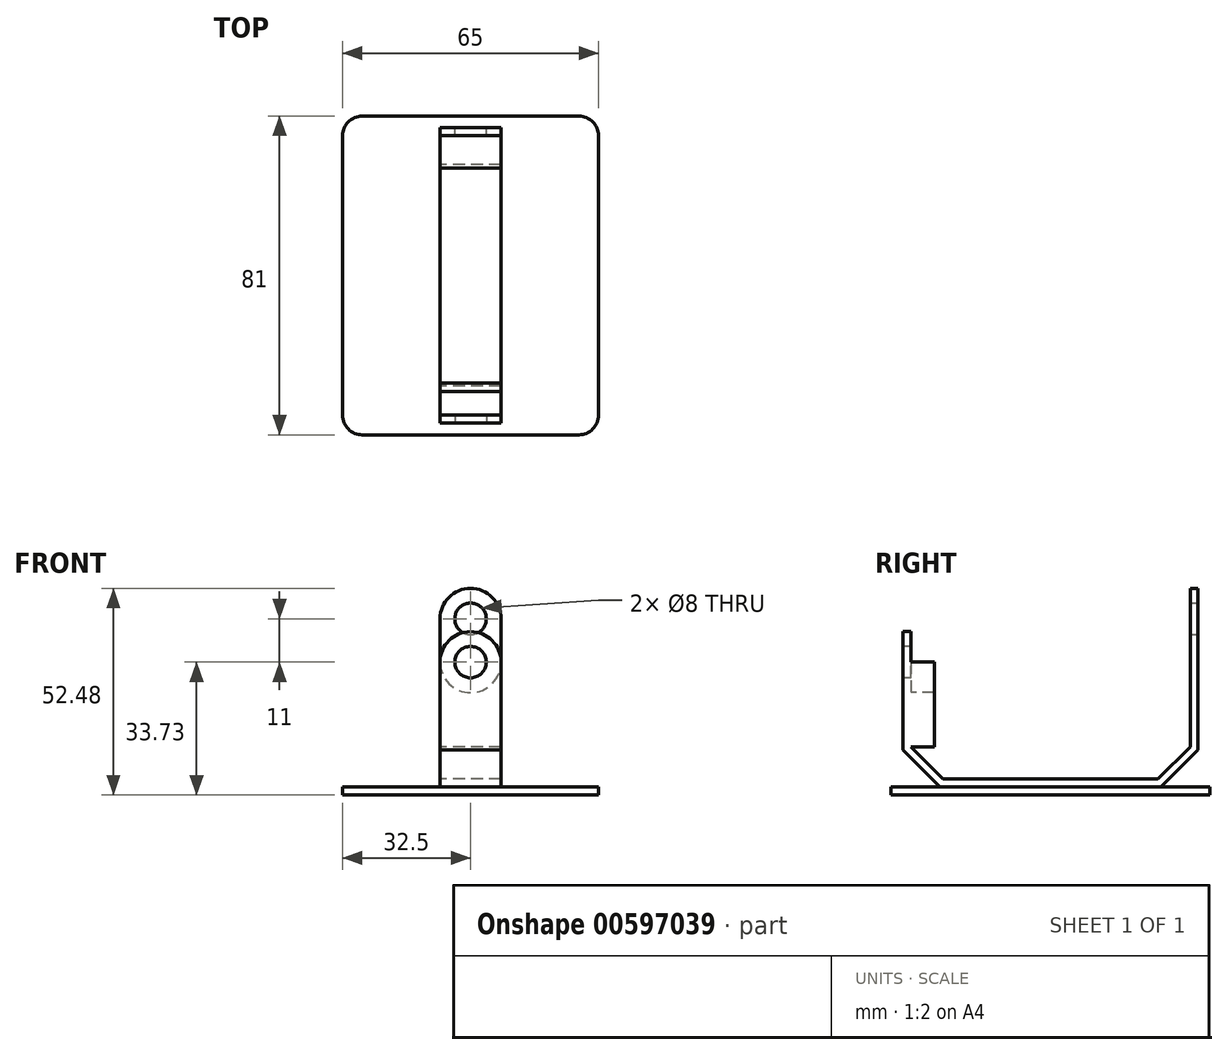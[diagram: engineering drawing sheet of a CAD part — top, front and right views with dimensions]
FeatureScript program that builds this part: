
annotation { "Feature Type Name" : "Feature", "Feature Type Description" : "" }
export const myFeature = defineFeature(function(context is Context, id is Id, definition is map)
    precondition{}
    {
        {
            var Q0;
            Q0=qCreatedBy(makeId("Right.planeOp"),FACE);
            var sketch = newSketch(context, id + "F0", { "sketchPlane" : qUnion([Q0])});
            skLineSegment(sketch, "E0", {"start": v(0, 21.5) * mm, "end": v(0, 0) * mm});
            skLineSegment(sketch, "E1", {"start": v(0, 0) * mm, "end": v(8.23, -8.23) * mm});
            skLineSegment(sketch, "E2", {"start": v(8.23, -8.23) * mm, "end": v(62.77, -8.23) * mm});
            skLineSegment(sketch, "E3", {"start": v(62.77, -8.23) * mm, "end": v(71, 0) * mm});
            skLineSegment(sketch, "E4", {"start": v(71, 0) * mm, "end": v(71, 32.5) * mm});
            skLineSegment(sketch, "E5", {"start": v(0, 21.5) * mm, "end": v(-2, 21.5) * mm});
            skLineSegment(sketch, "E6", {"start": v(73, 32.5) * mm, "end": v(71, 32.5) * mm});
            skLineSegment(sketch, "E7", {"start": v(-2, 21.5) * mm, "end": v(-2, -0.83) * mm});
            skLineSegment(sketch, "E8", {"start": v(-2, -0.83) * mm, "end": v(7.4, -10.23) * mm});
            skLineSegment(sketch, "E9", {"start": v(7.4, -10.23) * mm, "end": v(56.69, -10.23) * mm});
            skLineSegment(sketch, "E10", {"start": v(73, 32.5) * mm, "end": v(73, -0.83) * mm});
            skLineSegment(sketch, "E11", {"start": v(73, -0.83) * mm, "end": v(63.6, -10.23) * mm});
            skLineSegment(sketch, "E12", {"start": v(56.69, -10.23) * mm, "end": v(63.6, -10.23) * mm});
            skSolve(sketch);
        }
        {
            var Q0;
            Q0=makeQuery(id+"F0.imprint","IMPRINT",FACE,{"disambiguationData":[TD([[makeQuery(id+"F0.imprint","IMPRINT",EDGE,{"derivedFrom":sQuery(id+"F0.wireOp",EDGE,"E0")}),-1.0]])]});
            extrude(context, id + "F1", {"entities" : qUnion([Q0]), "endBound" : BoundingType.SYMMETRIC, "depth" : 15.5 * mm, "offsetDistance" : 25.4 * mm});
        }
        {
            var Q0;
            Q0=makeQuery(id+"F1.opExtrude","SWEPT_FACE",FACE,{"disambiguationData":[OSD([sQuery(id+"F0.wireOp",EDGE,"E7")])]});
            var sketch = newSketch(context, id + "F2", { "sketchPlane" : qUnion([Q0])});
            skArc(sketch, "E13", {"start": v(7.75, 21.5) * mm, "mid": v(0, 29.25) * mm, "end": v(-7.75, 21.5) * mm});
            skLineSegment(sketch, "E14", {"start": v(-7.75, 21.5) * mm, "end": v(7.75, 21.5) * mm});
            skSolve(sketch);
        }
        {
            var Q0;
            Q0=makeQuery(id+"F2.imprint","IMPRINT",FACE,{"disambiguationData":[TD([[makeQuery(id+"F2.imprint","IMPRINT",EDGE,{"derivedFrom":sQuery(id+"F2.wireOp",EDGE,"E13")}),1.0]])]});
            extrude(context, id + "F3", {"entities" : qUnion([Q0]), "operationType" : NewBodyOperationType.ADD, "oppositeDirection" : true, "depth" : 2 * mm, "offsetDistance" : 25.4 * mm});
        }
        {
            var Q0;
            Q0=makeQuery(id+"F3.boolean.opBoolean","MERGE",FACE,{"derivedFrom":[makeQuery(id+"F1.opExtrude","SWEPT_FACE",FACE,{"disambiguationData":[OSD([sQuery(id+"F0.wireOp",EDGE,"E7")])]}),makeQuery(id+"F3.opExtrude","CAP_FACE",FACE,{"disambiguationData":[OSD([sQuery(id+"F2.wireOp",EDGE,"E13"),sQuery(id+"F2.wireOp",EDGE,"E14")])],"isStart":true})]});
            var sketch = newSketch(context, id + "F4", { "sketchPlane" : qUnion([Q0])});
            skCircle(sketch, "E15", {"center": v(0, 21.5) * mm, "radius": 4 * mm});
            skSolve(sketch);
        }
        {
            var Q0;
            Q0=makeQuery(id+"F4.imprint","IMPRINT",FACE,{"disambiguationData":[TD([[makeQuery(id+"F4.imprint","IMPRINT",EDGE,{"derivedFrom":sQuery(id+"F4.wireOp",EDGE,"E15")}),1.0]])]});
            extrude(context, id + "F5", {"entities" : qUnion([Q0]), "operationType" : NewBodyOperationType.REMOVE, "oppositeDirection" : true, "depth" : 2 * mm, "offsetDistance" : 25.4 * mm});
        }
        {
            var Q0;
            Q0=makeQuery(id+"F3.boolean.opBoolean","MERGE",FACE,{"derivedFrom":[makeQuery(id+"F1.opExtrude","SWEPT_FACE",FACE,{"disambiguationData":[OSD([sQuery(id+"F0.wireOp",EDGE,"E0")])]}),makeQuery(id+"F3.opExtrude","CAP_FACE",FACE,{"disambiguationData":[OSD([sQuery(id+"F2.wireOp",EDGE,"E13"),sQuery(id+"F2.wireOp",EDGE,"E14")])],"isStart":false})]});
            var sketch = newSketch(context, id + "F6", { "sketchPlane" : qUnion([Q0])});
            skCircle(sketch, "E16", {"center": v(0, 21.5) * mm, "radius": 7.75 * mm});
            skCircle(sketch, "E17", {"center": v(0, 21.5) * mm, "radius": 4 * mm});
            skSolve(sketch);
        }
        {
            var Q0;
            {var subQ0=sQuery(id+"F6.wireOp",EDGE,"E16");Q0=makeQuery(id+"F6.imprint","IMPRINT",FACE,{"disambiguationData":[TD([[makeQuery(id+"F6.imprint","IMPRINT",EDGE,{"disambiguationData":[OD(0.0)],"derivedFrom":subQ0}),-1.0]])]});}
            extrude(context, id + "F7", {"entities" : qUnion([Q0]), "operationType" : NewBodyOperationType.ADD, "depth" : 6 * mm, "offsetDistance" : 25.4 * mm});
        }
        {
            var Q0;
            Q0=makeQuery(id+"F1.opExtrude","SWEPT_FACE",FACE,{"disambiguationData":[OSD([sQuery(id+"F0.wireOp",EDGE,"E10")])]});
            var sketch = newSketch(context, id + "F8", { "sketchPlane" : qUnion([Q0])});
            skArc(sketch, "E18", {"start": v(7.75, 32.5) * mm, "mid": v(0, 40.25) * mm, "end": v(-7.75, 32.5) * mm});
            skLineSegment(sketch, "E19", {"start": v(-7.75, 32.5) * mm, "end": v(7.75, 32.5) * mm});
            skSolve(sketch);
        }
        {
            var Q0;
            Q0 = qSketchRegion(id + "F8", true);
            extrude(context, id + "F9", {"entities" : qUnion([Q0]), "operationType" : NewBodyOperationType.ADD, "oppositeDirection" : true, "depth" : 2 * mm, "offsetDistance" : 25.4 * mm});
        }
        {
            var Q0;
            Q0=makeQuery(id+"F9.boolean.opBoolean","MERGE",FACE,{"derivedFrom":[makeQuery(id+"F1.opExtrude","SWEPT_FACE",FACE,{"disambiguationData":[OSD([sQuery(id+"F0.wireOp",EDGE,"E10")])]}),makeQuery(id+"F9.opExtrude","CAP_FACE",FACE,{"disambiguationData":[OSD([sQuery(id+"F8.wireOp",EDGE,"E18"),sQuery(id+"F8.wireOp",EDGE,"E19")])],"isStart":true})]});
            var sketch = newSketch(context, id + "F10", { "sketchPlane" : qUnion([Q0])});
            skCircle(sketch, "E20", {"center": v(0, 32.5) * mm, "radius": 4 * mm});
            skSolve(sketch);
        }
        {
            var Q0;
            Q0=makeQuery(id+"F10.imprint","IMPRINT",FACE,{"disambiguationData":[TD([[makeQuery(id+"F10.imprint","IMPRINT",EDGE,{"derivedFrom":sQuery(id+"F10.wireOp",EDGE,"E20")}),1.0]])]});
            extrude(context, id + "F11", {"entities" : qUnion([Q0]), "operationType" : NewBodyOperationType.REMOVE, "oppositeDirection" : true, "depth" : 2 * mm, "offsetDistance" : 25.4 * mm});
        }
        {
            var Q0;
            Q0=makeQuery(id+"F1.opExtrude","SWEPT_FACE",FACE,{"disambiguationData":[OSD([sQuery(id+"F0.wireOp",EDGE,"E9"),sQuery(id+"F0.wireOp",EDGE,"E12")])]});
            var sketch = newSketch(context, id + "F12", { "sketchPlane" : qUnion([Q0])});
            skLineSegment(sketch, "E21.bottom", {"start": v(-32.5, 5) * mm, "end": v(32.5, 5) * mm});
            skLineSegment(sketch, "E21.top", {"start": v(-32.5, -76) * mm, "end": v(32.5, -76) * mm});
            skLineSegment(sketch, "E21.left", {"start": v(-32.5, 5) * mm, "end": v(-32.5, -76) * mm});
            skLineSegment(sketch, "E21.right", {"start": v(32.5, 5) * mm, "end": v(32.5, -76) * mm});
            skPoint(sketch, "E21.middle", {"position": v(0, -35.5) * mm});
            skPoint(sketch, "E21.middle.positionSnap0", {"position": v(-7.75, -35.5) * mm});
            skPoint(sketch, "E21.middle.positionSnap1", {"position": v(0, -7.4) * mm});
            skPoint(sketch, "E21.centerSnap0", {"position": v(-7.75, -35.5) * mm});
            skPoint(sketch, "E21.centerSnap1", {"position": v(0, -7.4) * mm});
            skSolve(sketch);
        }
        {
            var Q0;
            {var subQ0=sQuery(id+"F0.wireOp",EDGE,"E9");Q0=makeQuery(id+"F12.imprint","IMPRINT",FACE,{"disambiguationData":[TD([[makeQuery(id+"F12.imprint","IMPRINT",EDGE,{"derivedFrom":makeQuery(id+"F1.opExtrude","SWEPT_EDGE",EDGE,{"disambiguationData":[OSD([sQuery(id+"F0.wireOp",EDGE,"E8"),subQ0])]})}),1.0]])]});}
            var Q1;
            Q1=makeQuery(id+"F12.imprint","IMPRINT",FACE,{"disambiguationData":[TD([[makeQuery(id+"F12.imprint","IMPRINT",EDGE,{"derivedFrom":sQuery(id+"F12.wireOp",EDGE,"E21.bottom")}),-1.0]])]});
            extrude(context, id + "F13", {"entities" : qUnion([Q0, Q1]), "operationType" : NewBodyOperationType.ADD, "depth" : 2 * mm, "offsetDistance" : 25.4 * mm});
        }
        {
            var Q0;
            Q0=makeQuery(id+"F13.opExtrude","SWEPT_EDGE",EDGE,{"disambiguationData":[OSD([sQuery(id+"F12.wireOp",EDGE,"E21.bottom"),sQuery(id+"F12.wireOp",EDGE,"E21.right")])]});
            var Q1;
            Q1=makeQuery(id+"F13.opExtrude","SWEPT_EDGE",EDGE,{"disambiguationData":[OSD([sQuery(id+"F12.wireOp",EDGE,"E21.bottom"),sQuery(id+"F12.wireOp",EDGE,"E21.left")])]});
            var Q2;
            Q2=makeQuery(id+"F13.opExtrude","SWEPT_EDGE",EDGE,{"disambiguationData":[OSD([sQuery(id+"F12.wireOp",EDGE,"E21.top"),sQuery(id+"F12.wireOp",EDGE,"E21.left")])]});
            var Q3;
            Q3=makeQuery(id+"F13.opExtrude","SWEPT_EDGE",EDGE,{"disambiguationData":[OSD([sQuery(id+"F12.wireOp",EDGE,"E21.top"),sQuery(id+"F12.wireOp",EDGE,"E21.right")])]});
            fillet(context, id + "F14", {"entities" : qUnion([Q0, Q1, Q2, Q3]), "radius" : 5 * mm, "tangentPropagation" : true, "allowEdgeOverflow" : false});
        }
    });
